# Revit family: SH-1097-E27
name_source: partatom
category: Lighting Fixtures
revit_build: Autodesk Revit 2017 (Build: 20160225_1515(x64)
units: mm (PartAtom-declared; Revit-internal decimal feet)

## family parameters
Cut with Voids When Loaded = No
Host = Face
Light Source = Yes
Part Type = Normal
Room Calculation Point = No
Round Connector Dimension = Use Diameter
Shared = No

## types (2) — shared parameters
Body Material = Aluminum
Color Filter = 16777215
Default Elevation = 122 cm
Diffuser Material = Glass
Dimming Lamp Color Temperature Shift = <None>
IP = IP55
Lamp = E40
Manufacturer = SHOA
Model = SH-1097
Number of lamps = 1
Photometric Web File = 50W_IESNA2002(1).IES
Protection Class = Class I
Tilt Angle = 90.00°
URL = https://www.shoaco.com
website = www.shoaco.com

## per-type parameters (varying)
| type | Voltage/Frequency | Wattage. | consumption current |
| SH-1097(Black color-3000K-E40-150w) | 220V/50Hz | 150 W | 2 A |
| SH-1097(Black color-3000K-E40-250w) | 220V/60Hz | 250 W | 3 A |

## geometry (parser evidence)
native form markers: Sweep x2
no freeform markers — native parametric forms only
